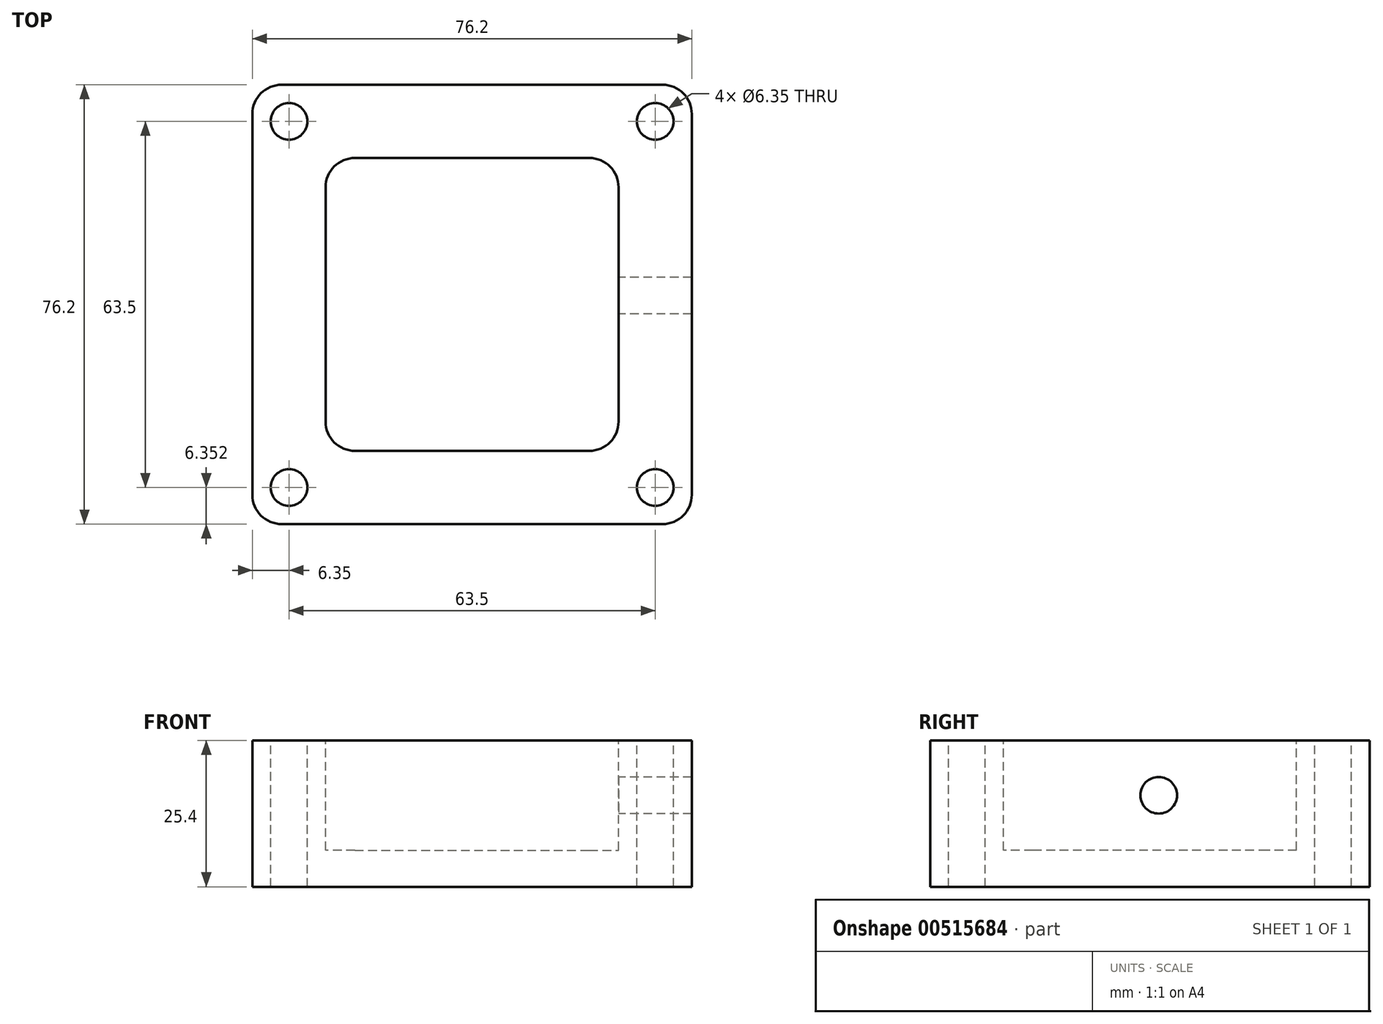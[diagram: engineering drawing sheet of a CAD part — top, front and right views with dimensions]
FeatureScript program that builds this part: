
annotation { "Feature Type Name" : "Feature", "Feature Type Description" : "" }
export const myFeature = defineFeature(function(context is Context, id is Id, definition is map)
    precondition{}
    {
        {
            var Q0;
            Q0=qCreatedBy(makeId("Top.planeOp"),FACE);
            var sketch = newSketch(context, id + "F0", { "sketchPlane" : qUnion([Q0])});
            skLineSegment(sketch, "E0.bottom", {"start": v(-38.35, 36.6) * mm, "end": v(37.85, 36.6) * mm});
            skLineSegment(sketch, "E0.top", {"start": v(-38.35, -39.6) * mm, "end": v(37.85, -39.6) * mm});
            skLineSegment(sketch, "E0.left", {"start": v(-38.35, 36.6) * mm, "end": v(-38.35, -39.6) * mm});
            skLineSegment(sketch, "E0.right", {"start": v(37.85, 36.6) * mm, "end": v(37.85, -39.6) * mm});
            skSolve(sketch);
        }
        {
            var Q0;
            Q0 = qSketchRegion(id + "F0", true);
            extrude(context, id + "F1", {"entities" : qUnion([Q0]), "depth" : 25.4 * mm, "offsetDistance" : 25.4 * mm});
        }
        {
            var Q0;
            Q0=makeQuery(id+"F1.opExtrude","CAP_FACE",FACE,{"disambiguationData":[OSD([sQuery(id+"F0.wireOp",EDGE,"E0.bottom"),sQuery(id+"F0.wireOp",EDGE,"E0.top"),sQuery(id+"F0.wireOp",EDGE,"E0.left"),sQuery(id+"F0.wireOp",EDGE,"E0.right")])],"isStart":false});
            var sketch = newSketch(context, id + "F2", { "sketchPlane" : qUnion([Q0])});
            skLineSegment(sketch, "E1.bottom", {"start": v(-25.65, 23.9) * mm, "end": v(25.15, 23.9) * mm});
            skLineSegment(sketch, "E1.top", {"start": v(-25.65, -26.9) * mm, "end": v(25.15, -26.9) * mm});
            skLineSegment(sketch, "E1.left", {"start": v(-25.65, 23.9) * mm, "end": v(-25.65, -26.9) * mm});
            skLineSegment(sketch, "E1.right", {"start": v(25.15, 23.9) * mm, "end": v(25.15, -26.9) * mm});
            skLineSegment(sketch, "E2", {"start": v(37.85, -39.6) * mm, "end": v(25.15, -26.9) * mm, "construction": true});
            skLineSegment(sketch, "E3", {"start": v(37.85, 36.6) * mm, "end": v(25.15, 23.9) * mm, "construction": true});
            skLineSegment(sketch, "E4", {"start": v(-25.65, 23.9) * mm, "end": v(-38.35, 36.6) * mm, "construction": true});
            skLineSegment(sketch, "E5", {"start": v(-38.35, -39.6) * mm, "end": v(-25.65, -26.9) * mm, "construction": true});
            skCircle(sketch, "E6", {"center": v(-32, -33.25) * mm, "radius": 3.18 * mm});
            skCircle(sketch, "E7", {"center": v(31.5, -33.25) * mm, "radius": 3.18 * mm});
            skCircle(sketch, "E8", {"center": v(31.5, 30.25) * mm, "radius": 3.18 * mm});
            skCircle(sketch, "E9", {"center": v(-32, 30.25) * mm, "radius": 3.18 * mm});
            skSolve(sketch);
        }
        {
            var Q0;
            Q0 = qSketchRegion(id + "F2", true);
            var Q1;
            Q1=makeQuery(id+"F1.opExtrude","CAP_FACE",FACE,{"disambiguationData":[OSD([sQuery(id+"F0.wireOp",EDGE,"E0.bottom"),sQuery(id+"F0.wireOp",EDGE,"E0.top"),sQuery(id+"F0.wireOp",EDGE,"E0.left"),sQuery(id+"F0.wireOp",EDGE,"E0.right")])],"isStart":true});
            extrude(context, id + "F3", {"entities" : qUnion([Q0]), "operationType" : NewBodyOperationType.REMOVE, "oppositeDirection" : true, "depth" : 19.05 * mm, "endBoundEntityFace" : qUnion([Q1]), "offsetDistance" : 25.4 * mm});
        }
        {
            var Q0;
            Q0=makeQuery(id+"F1.opExtrude","SWEPT_EDGE",EDGE,{"disambiguationData":[OSD([sQuery(id+"F0.wireOp",EDGE,"E0.bottom"),sQuery(id+"F0.wireOp",EDGE,"E0.left")])]});
            var Q1;
            Q1=makeQuery(id+"F1.opExtrude","SWEPT_EDGE",EDGE,{"disambiguationData":[OSD([sQuery(id+"F0.wireOp",EDGE,"E0.bottom"),sQuery(id+"F0.wireOp",EDGE,"E0.right")])]});
            var Q2;
            Q2=makeQuery(id+"F1.opExtrude","SWEPT_EDGE",EDGE,{"disambiguationData":[OSD([sQuery(id+"F0.wireOp",EDGE,"E0.top"),sQuery(id+"F0.wireOp",EDGE,"E0.right")])]});
            var Q3;
            Q3=makeQuery(id+"F1.opExtrude","SWEPT_EDGE",EDGE,{"disambiguationData":[OSD([sQuery(id+"F0.wireOp",EDGE,"E0.top"),sQuery(id+"F0.wireOp",EDGE,"E0.left")])]});
            var Q4;
            Q4=makeQuery(id+"F3.boolean.opBoolean","COPY",EDGE,{"derivedFrom":makeQuery(id+"F3.opExtrude","SWEPT_EDGE",EDGE,{"disambiguationData":[OSD([sQuery(id+"F2.wireOp",EDGE,"E1.bottom"),sQuery(id+"F2.wireOp",EDGE,"E1.right")])]})});
            var Q5;
            Q5=makeQuery(id+"F3.boolean.opBoolean","COPY",EDGE,{"derivedFrom":makeQuery(id+"F3.opExtrude","SWEPT_EDGE",EDGE,{"disambiguationData":[OSD([sQuery(id+"F2.wireOp",EDGE,"E1.top"),sQuery(id+"F2.wireOp",EDGE,"E1.right")])]})});
            var Q6;
            Q6=makeQuery(id+"F3.boolean.opBoolean","COPY",EDGE,{"derivedFrom":makeQuery(id+"F3.opExtrude","SWEPT_EDGE",EDGE,{"disambiguationData":[OSD([sQuery(id+"F2.wireOp",EDGE,"E1.top"),sQuery(id+"F2.wireOp",EDGE,"E1.left")])]})});
            var Q7;
            Q7=makeQuery(id+"F3.boolean.opBoolean","COPY",EDGE,{"derivedFrom":makeQuery(id+"F3.opExtrude","SWEPT_EDGE",EDGE,{"disambiguationData":[OSD([sQuery(id+"F2.wireOp",EDGE,"E1.bottom"),sQuery(id+"F2.wireOp",EDGE,"E1.left")])]})});
            fillet(context, id + "F4", {"entities" : qUnion([Q0, Q1, Q2, Q3, Q4, Q5, Q6, Q7]), "radius" : 5.08 * mm, "tangentPropagation" : true, "allowEdgeOverflow" : false});
        }
        {
            var Q0;
            Q0=makeQuery(id+"F3.boolean.opBoolean","COPY",FACE,{"derivedFrom":makeQuery(id+"F3.opExtrude","SWEPT_FACE",FACE,{"disambiguationData":[OSD([sQuery(id+"F2.wireOp",EDGE,"E1.right")])]})});
            var sketch = newSketch(context, id + "F5", { "sketchPlane" : qUnion([Q0])});
            skCircle(sketch, "E10", {"center": v(0, 15.88) * mm, "radius": 3.18 * mm});
            skPoint(sketch, "E10.centerSnap0", {"position": v(21.82, 15.88) * mm});
            skSolve(sketch);
        }
        {
            var Q0;
            Q0 = qSketchRegion(id + "F5", true);
            var Q1;
            Q1=makeQuery(id+"F1.opExtrude","SWEPT_FACE",FACE,{"disambiguationData":[OSD([sQuery(id+"F0.wireOp",EDGE,"E0.right")])]});
            extrude(context, id + "F6", {"entities" : qUnion([Q0]), "operationType" : NewBodyOperationType.REMOVE, "endBound" : BoundingType.UP_TO_SURFACE, "oppositeDirection" : true, "depth" : 25.4 * mm, "endBoundEntityFace" : qUnion([Q1]), "offsetDistance" : 25.4 * mm});
        }
        {
            var Q0;
            Q0=makeQuery(id+"F3.boolean.opBoolean","COPY",FACE,{"derivedFrom":makeQuery(id+"F3.opExtrude","CAP_FACE",FACE,{"disambiguationData":[OSD([sQuery(id+"F2.wireOp",EDGE,"E8")])],"isStart":false})});
            var Q1;
            Q1=makeQuery(id+"F3.boolean.opBoolean","COPY",FACE,{"derivedFrom":makeQuery(id+"F3.opExtrude","CAP_FACE",FACE,{"disambiguationData":[OSD([sQuery(id+"F2.wireOp",EDGE,"E7")])],"isStart":false})});
            var Q2;
            Q2=makeQuery(id+"F3.boolean.opBoolean","COPY",FACE,{"derivedFrom":makeQuery(id+"F3.opExtrude","CAP_FACE",FACE,{"disambiguationData":[OSD([sQuery(id+"F2.wireOp",EDGE,"E9")])],"isStart":false})});
            var Q3;
            Q3=makeQuery(id+"F3.boolean.opBoolean","COPY",FACE,{"derivedFrom":makeQuery(id+"F3.opExtrude","CAP_FACE",FACE,{"disambiguationData":[OSD([sQuery(id+"F2.wireOp",EDGE,"E6")])],"isStart":false})});
            var Q4;
            Q4=makeQuery(id+"F1.opExtrude","CAP_FACE",FACE,{"disambiguationData":[OSD([sQuery(id+"F0.wireOp",EDGE,"E0.bottom"),sQuery(id+"F0.wireOp",EDGE,"E0.top"),sQuery(id+"F0.wireOp",EDGE,"E0.left"),sQuery(id+"F0.wireOp",EDGE,"E0.right")])],"isStart":true});
            extrude(context, id + "F7", {"entities" : qUnion([Q0, Q1, Q2, Q3]), "operationType" : NewBodyOperationType.REMOVE, "endBound" : BoundingType.UP_TO_SURFACE, "oppositeDirection" : true, "depth" : 25.4 * mm, "endBoundEntityFace" : qUnion([Q4]), "offsetDistance" : 25.4 * mm});
        }
    });
